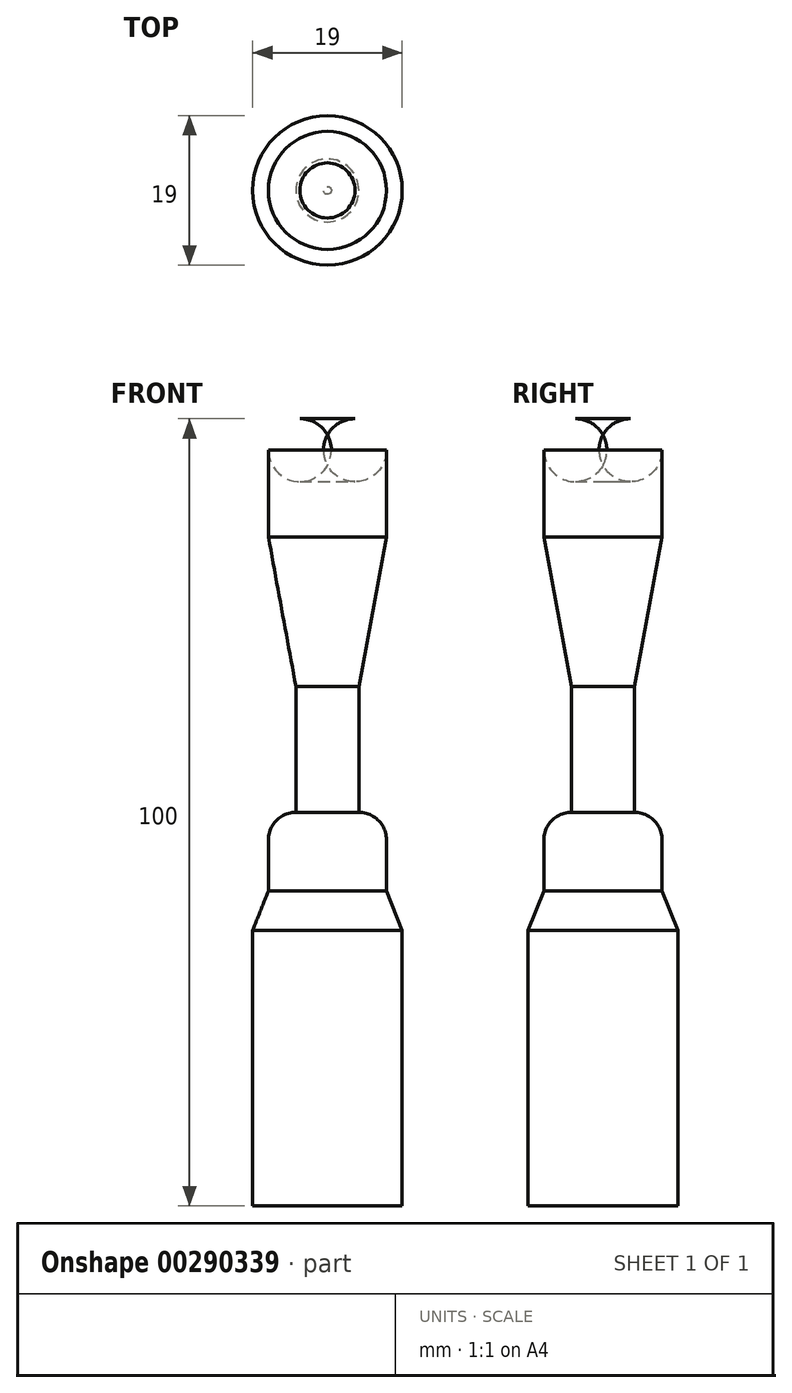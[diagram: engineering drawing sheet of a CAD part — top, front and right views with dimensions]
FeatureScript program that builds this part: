
annotation { "Feature Type Name" : "Feature", "Feature Type Description" : "" }
export const myFeature = defineFeature(function(context is Context, id is Id, definition is map)
    precondition{}
    {
        {
            var Q0;
            Q0=qCreatedBy(makeId("Front.planeOp"),FACE);
            var sketch = newSketch(context, id + "F0", { "sketchPlane" : qUnion([Q0])});
            skLineSegment(sketch, "E0", {"start": v(0, 0) * mm, "end": v(3.5, 0) * mm});
            skArc(sketch, "E1", {"start": v(7.5, -4) * mm, "mid": v(6.33, -1.17) * mm, "end": v(3.5, 0) * mm});
            skLineSegment(sketch, "E2", {"start": v(7.5, -4) * mm, "end": v(7.5, -15) * mm});
            skLineSegment(sketch, "E3", {"start": v(7.5, -15) * mm, "end": v(4, -34) * mm});
            skLineSegment(sketch, "E4", {"start": v(4, -34) * mm, "end": v(4, -50) * mm});
            skLineSegment(sketch, "E5", {"start": v(7.5, -53.5) * mm, "end": v(7.5, -60) * mm});
            skLineSegment(sketch, "E6", {"start": v(7.5, -60) * mm, "end": v(9.5, -65) * mm});
            skLineSegment(sketch, "E7", {"start": v(9.5, -65) * mm, "end": v(9.5, -100) * mm});
            skLineSegment(sketch, "E8", {"start": v(9.5, -100) * mm, "end": v(0, -100) * mm});
            skLineSegment(sketch, "E9", {"start": v(0, -100) * mm, "end": v(0, 0) * mm});
            skArc(sketch, "E10", {"start": v(7.5, -53.5) * mm, "mid": v(6.47, -51.03) * mm, "end": v(4, -50) * mm});
            skSolve(sketch);
        }
        {
            var Q0;
            Q0=makeQuery(id+"F0.imprint","IMPRINT",FACE,{"disambiguationData":[TD([[makeQuery(id+"F0.imprint","IMPRINT",EDGE,{"derivedFrom":sQuery(id+"F0.wireOp",EDGE,"E0")}),-1.0]])]});
            var Q1;
            Q1=sQuery(id+"F0.wireOp",EDGE,"E9");
            revolve(context, id + "F1", {"entities" : qUnion([Q0]), "axis" : qUnion([Q1]), "revolveType" : RevolveType.FULL});
        }
    });
